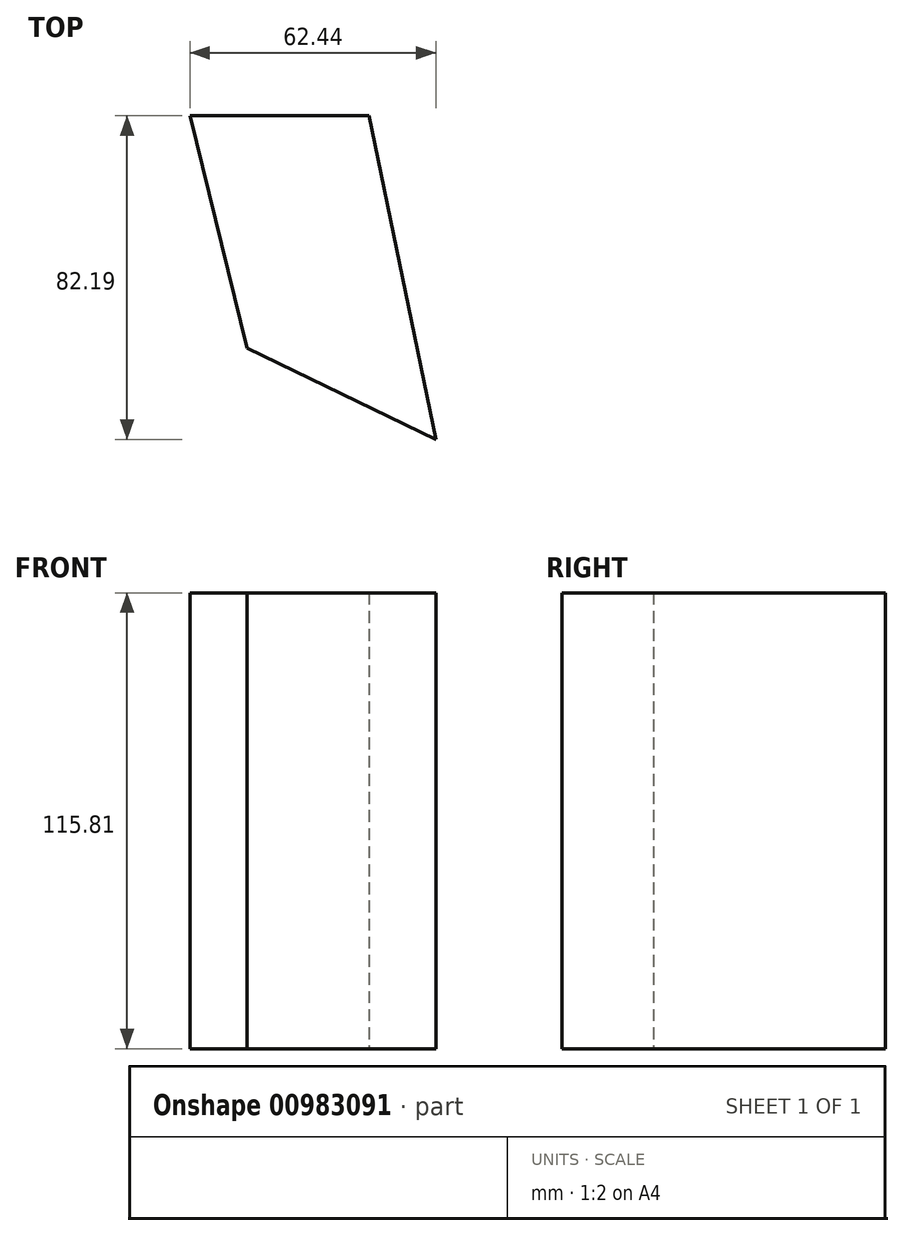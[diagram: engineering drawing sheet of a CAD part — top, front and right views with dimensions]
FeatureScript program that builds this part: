
annotation { "Feature Type Name" : "Feature", "Feature Type Description" : "" }
export const myFeature = defineFeature(function(context is Context, id is Id, definition is map)
    precondition{}
    {
        {
            var Q0;
            Q0=qCreatedBy(makeId("Top.planeOp"),FACE);
            var sketch = newSketch(context, id + "F0", { "sketchPlane" : qUnion([Q0])});
            skLineSegment(sketch, "E0", {"start": v(45.4, 55.6) * mm, "end": v(0, 55.6) * mm});
            skLineSegment(sketch, "E1", {"start": v(0, 55.6) * mm, "end": v(14.49, -3.35) * mm});
            skLineSegment(sketch, "E2", {"start": v(14.49, -3.35) * mm, "end": v(62.44, -26.6) * mm});
            skLineSegment(sketch, "E3", {"start": v(62.44, -26.6) * mm, "end": v(45.4, 55.6) * mm});
            skSolve(sketch);
        }
        {
            var Q0;
            Q0=makeQuery(id+"F0.imprint","IMPRINT",FACE,{"disambiguationData":[TD([[makeQuery(id+"F0.imprint","IMPRINT",EDGE,{"derivedFrom":sQuery(id+"F0.wireOp",EDGE,"E0")}),1.0]])]});
            extrude(context, id + "F1", {"entities" : qUnion([Q0]), "depth" : 115.81 * mm, "offsetDistance" : 25.4 * mm});
        }
    });
